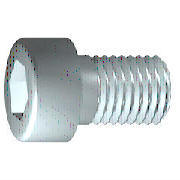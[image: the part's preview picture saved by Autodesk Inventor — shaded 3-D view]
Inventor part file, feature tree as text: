
AUTODESK INVENTOR PART (.ipt)
format: ipt  version: 2023.3 (Build 273359000, 359)  size: 198,144 bytes
history: native  units: mm (DEFAULTED — no unit token found)
features: sketch x2, other x1, extrude x1, plane x1, fillet x1
ambient origin geometry x7: Origin, YZ Plane, XY Plane, X Axis, Y Axis, Z Axis, Center Point
bodies: Solid1 (feature_tree)
feature tree (6):
  other  "Körper"
  extrude  "Loch"  Depth=2.0mm
  plane  "Work Plane1"
  fillet  "Fillet2"  Radius=2.0mm
  sketch  "Skizze1"  dims[d1=2.0mm d2=0.24548mm d3=2.0mm]
  sketch  "Skizze2"  dims[d4=1.0mm d5=60.0deg d6=2.0mm d7=2.0mm d8=1.732051mm d9=3.8mm d10=90.0deg d11=10.0mm d12=0.0mm d13=2.0mm d14=0.0mm d15=0.24538mm d16=0.24538mm d17=0.2mm d19=0.0mm d26=3.0mm d27=45.0deg d28=0.0mm d29=0.0mm d30=0.1mm]
